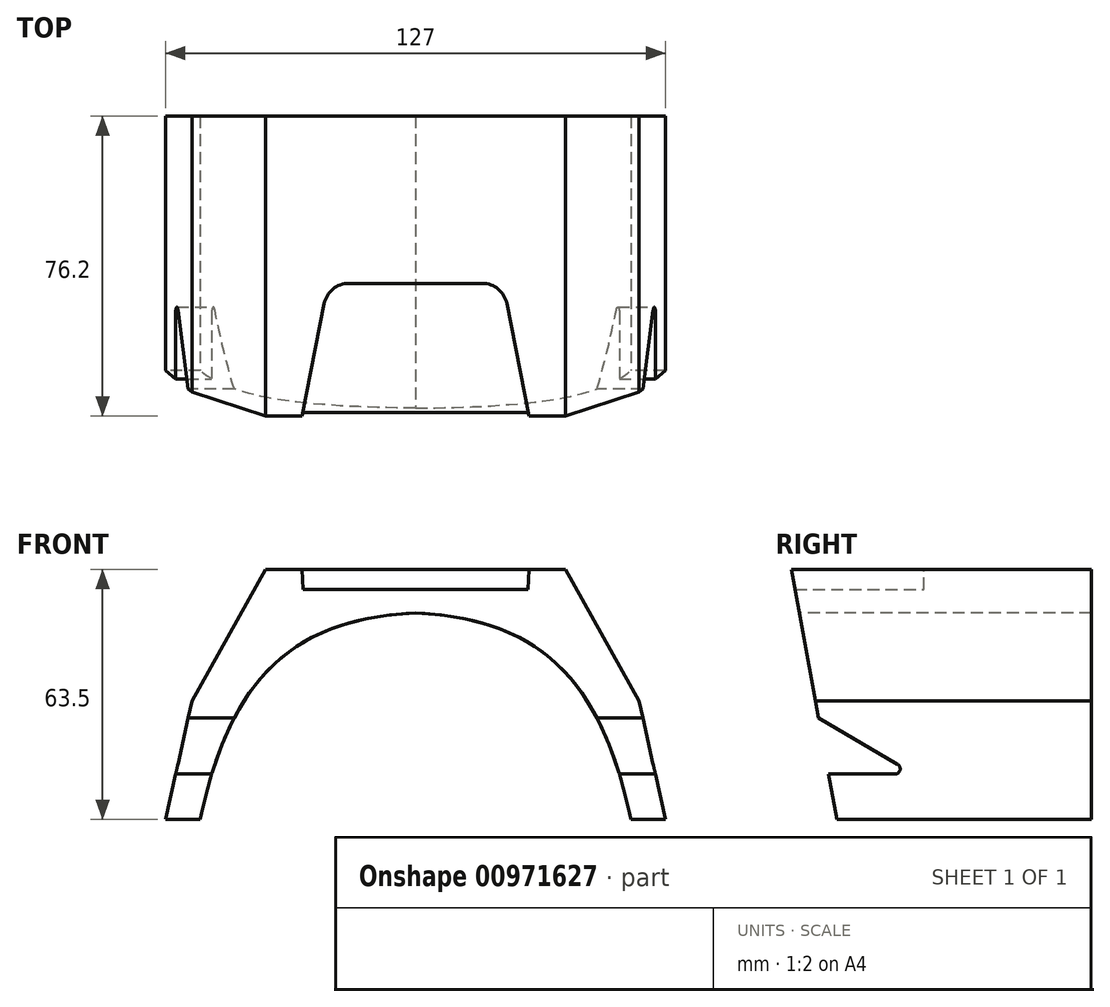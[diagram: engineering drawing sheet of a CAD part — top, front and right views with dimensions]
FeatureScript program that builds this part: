
annotation { "Feature Type Name" : "Feature", "Feature Type Description" : "" }
export const myFeature = defineFeature(function(context is Context, id is Id, definition is map)
    precondition{}
    {
        {
            var Q0;
            Q0=qCreatedBy(makeId("Front.planeOp"),FACE);
            var sketch = newSketch(context, id + "F0", { "sketchPlane" : qUnion([Q0])});
            skLineSegment(sketch, "E0", {"start": v(0, 33.34) * mm, "end": v(-38.1, 33.34) * mm});
            skLineSegment(sketch, "E1", {"start": v(-38.1, 33.34) * mm, "end": v(-56.8, 0) * mm});
            skLineSegment(sketch, "E2", {"start": v(-56.8, 0) * mm, "end": v(-63.5, -30.16) * mm});
            skLineSegment(sketch, "E3", {"start": v(-63.5, -30.16) * mm, "end": v(0, -30.16) * mm});
            skLineSegment(sketch, "E4.MirrorCS", {"start": v(0, 33.34) * mm, "end": v(38.1, 33.34) * mm});
            skLineSegment(sketch, "E5.MirrorCS", {"start": v(38.1, 33.34) * mm, "end": v(56.8, 0) * mm});
            skLineSegment(sketch, "E6.MirrorCS", {"start": v(56.8, 0) * mm, "end": v(63.5, -30.16) * mm});
            skLineSegment(sketch, "E7.MirrorCS", {"start": v(63.5, -30.16) * mm, "end": v(0, -30.16) * mm});
            skSolve(sketch);
        }
        {
            var Q0;
            Q0=makeQuery(id+"F0.imprint","IMPRINT",FACE,{"disambiguationData":[TD([[makeQuery(id+"F0.imprint","IMPRINT",EDGE,{"derivedFrom":sQuery(id+"F0.wireOp",EDGE,"E0")}),1.0]])]});
            extrude(context, id + "F1", {"entities" : qUnion([Q0]), "depth" : 76.2 * mm, "offsetDistance" : 25.4 * mm});
        }
        {
            var Q0;
            Q0=makeQuery(id+"F1.opExtrude","CAP_FACE",FACE,{"disambiguationData":[OSD([sQuery(id+"F0.wireOp",EDGE,"E0"),sQuery(id+"F0.wireOp",EDGE,"E1"),sQuery(id+"F0.wireOp",EDGE,"E2"),sQuery(id+"F0.wireOp",EDGE,"E3"),sQuery(id+"F0.wireOp",EDGE,"E4.MirrorCS"),sQuery(id+"F0.wireOp",EDGE,"E5.MirrorCS"),sQuery(id+"F0.wireOp",EDGE,"E6.MirrorCS"),sQuery(id+"F0.wireOp",EDGE,"E7.MirrorCS")])],"isStart":false});
            var sketch = newSketch(context, id + "F2", { "sketchPlane" : qUnion([Q0])});
            skFitSpline(sketch, "E8", {"points": [v(0, 22.3) * mm, v(-54.7, -30.16) * mm], "startDerivative": vector(-87.83, -4.49) * mm, "endDerivative": vector(-23.7, -114.46) * mm});
            skFitSpline(sketch, "E9.MirrorCS", {"points": [v(0, 22.3) * mm, v(54.7, -30.16) * mm], "startDerivative": vector(87.83, -4.49) * mm, "endDerivative": vector(23.7, -114.46) * mm});
            skLineSegment(sketch, "E10", {"start": v(-54.7, -30.16) * mm, "end": v(54.7, -30.16) * mm});
            skSolve(sketch);
        }
        {
            var Q0;
            Q0=makeQuery(id+"F2.imprint","IMPRINT",FACE,{"disambiguationData":[TD([[makeQuery(id+"F2.imprint","IMPRINT",EDGE,{"derivedFrom":sQuery(id+"F2.wireOp",EDGE,"E8")}),1.0]])]});
            extrude(context, id + "F3", {"entities" : qUnion([Q0]), "operationType" : NewBodyOperationType.REMOVE, "oppositeDirection" : true, "depth" : 115.06 * mm, "offsetDistance" : 25.4 * mm});
        }
        {
            var Q0;
            Q0=makeQuery(id+"F1.opExtrude","SWEPT_FACE",FACE,{"disambiguationData":[OSD([sQuery(id+"F0.wireOp",EDGE,"E0"),sQuery(id+"F0.wireOp",EDGE,"E4.MirrorCS")])]});
            var sketch = newSketch(context, id + "F4", { "sketchPlane" : qUnion([Q0])});
            skLineSegment(sketch, "E11", {"start": v(-28.79, -76.2) * mm, "end": v(-23.18, -47.63) * mm});
            skLineSegment(sketch, "E12", {"start": v(-16.95, -42.5) * mm, "end": v(0, -42.5) * mm});
            skLineSegment(sketch, "E13.MirrorCS", {"start": v(16.95, -42.5) * mm, "end": v(0, -42.5) * mm});
            skLineSegment(sketch, "E14.MirrorCS", {"start": v(28.79, -76.2) * mm, "end": v(23.18, -47.63) * mm});
            skPoint(sketch, "E15.visualSharp", {"position": v(-22.18, -42.5) * mm});
            skArc(sketch, "E15.filletArc", {"start": v(-16.95, -42.5) * mm, "mid": v(-20.99, -43.95) * mm, "end": v(-23.18, -47.63) * mm});
            skPoint(sketch, "E16.visualSharp", {"position": v(22.18, -42.5) * mm});
            skArc(sketch, "E16.filletArc", {"start": v(23.18, -47.63) * mm, "mid": v(20.99, -43.95) * mm, "end": v(16.95, -42.5) * mm});
            skSolve(sketch);
        }
        {
            var Q0;
            {var subQ1=sQuery(id+"F4.wireOp",EDGE,"E11");Q0=makeQuery(id+"F4.imprint","IMPRINT",FACE,{"disambiguationData":[TD([[makeQuery(id+"F4.imprint","IMPRINT",EDGE,{"derivedFrom":subQ1}),-1.0]])]});}
            extrude(context, id + "F5", {"entities" : qUnion([Q0]), "operationType" : NewBodyOperationType.REMOVE, "oppositeDirection" : true, "depth" : 5.08 * mm, "offsetDistance" : 25.4 * mm});
        }
        {
            var Q0;
            Q0=qCreatedBy(makeId("Right.planeOp"),FACE);
            var sketch = newSketch(context, id + "F6", { "sketchPlane" : qUnion([Q0])});
            skLineSegment(sketch, "E17", {"start": v(-78.21, -18.64) * mm, "end": v(-49.9, -18.64) * mm});
            skLineSegment(sketch, "E18", {"start": v(-49.23, -16.15) * mm, "end": v(-80.73, 2.37) * mm});
            skLineSegment(sketch, "E19", {"start": v(-80.73, 2.37) * mm, "end": v(-78.21, -18.64) * mm});
            skArc(sketch, "E20", {"start": v(-49.9, -18.64) * mm, "mid": v(-48.61, -17.65) * mm, "end": v(-49.23, -16.15) * mm});
            skSolve(sketch);
        }
        {
            var Q0;
            Q0=makeQuery(id+"F6.imprint","IMPRINT",FACE,{"disambiguationData":[TD([[makeQuery(id+"F6.imprint","IMPRINT",EDGE,{"derivedFrom":sQuery(id+"F6.wireOp",EDGE,"E17")}),1.0]])]});
            extrude(context, id + "F7", {"entities" : qUnion([Q0]), "operationType" : NewBodyOperationType.REMOVE, "endBound" : BoundingType.SYMMETRIC, "oppositeDirection" : true, "depth" : 203.2 * mm, "offsetDistance" : 25.4 * mm});
        }
        {
            var Q0;
            Q0=qCreatedBy(makeId("Right.planeOp"),FACE);
            var sketch = newSketch(context, id + "F8", { "sketchPlane" : qUnion([Q0])});
            skLineSegment(sketch, "E21", {"start": v(-63.57, -36.22) * mm, "end": v(-76.25, 33.6) * mm});
            skLineSegment(sketch, "E22", {"start": v(-76.25, 33.6) * mm, "end": v(-85.85, -35.24) * mm});
            skLineSegment(sketch, "E23", {"start": v(-85.85, -35.24) * mm, "end": v(-63.57, -36.22) * mm});
            skSolve(sketch);
        }
        {
            var Q0;
            Q0=makeQuery(id+"F8.imprint","IMPRINT",FACE,{"disambiguationData":[TD([[makeQuery(id+"F8.imprint","IMPRINT",EDGE,{"derivedFrom":sQuery(id+"F8.wireOp",EDGE,"E21")}),1.0]])]});
            extrude(context, id + "F9", {"entities" : qUnion([Q0]), "operationType" : NewBodyOperationType.REMOVE, "endBound" : BoundingType.SYMMETRIC, "oppositeDirection" : true, "depth" : 203.2 * mm, "offsetDistance" : 25.4 * mm});
        }
    });
